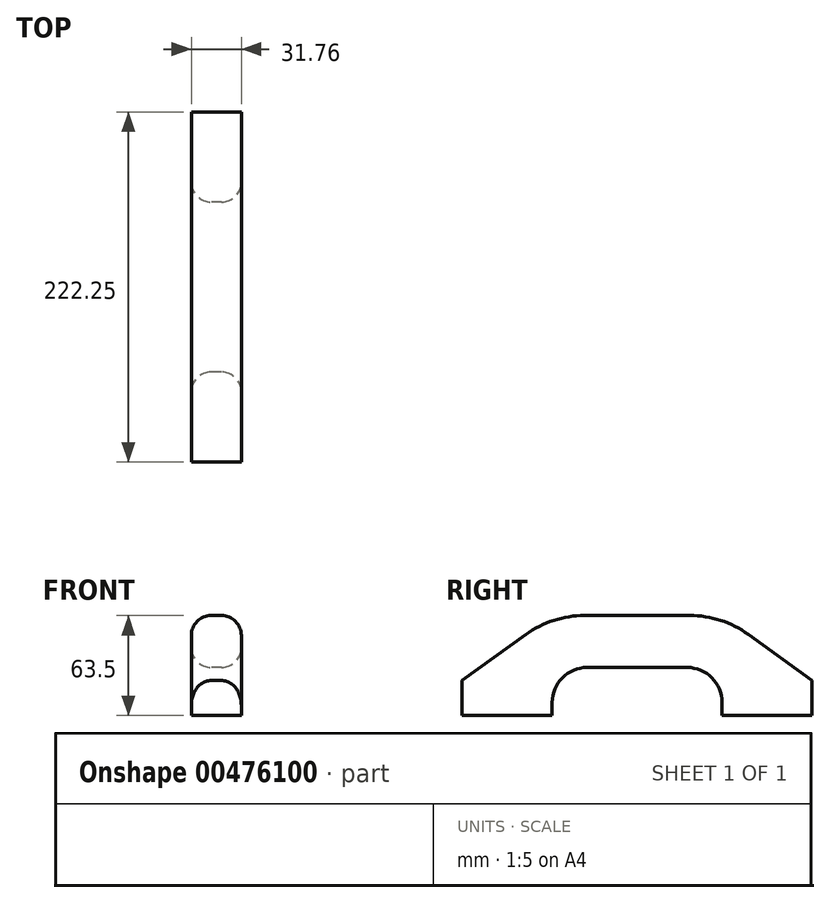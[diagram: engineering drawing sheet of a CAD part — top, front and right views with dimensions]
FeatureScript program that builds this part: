
annotation { "Feature Type Name" : "Feature", "Feature Type Description" : "" }
export const myFeature = defineFeature(function(context is Context, id is Id, definition is map)
    precondition{}
    {
        {
            var Q0;
            Q0=qCreatedBy(makeId("Right.planeOp"),FACE);
            var sketch = newSketch(context, id + "F0", { "sketchPlane" : qUnion([Q0])});
            skLineSegment(sketch, "E0", {"start": v(0, 0) * mm, "end": v(57.15, 0) * mm});
            skLineSegment(sketch, "E1", {"start": v(0, 0) * mm, "end": v(0, 22.23) * mm});
            skLineSegment(sketch, "E2", {"start": v(222.25, 0) * mm, "end": v(222.25, 22.23) * mm});
            skLineSegment(sketch, "E3", {"start": v(57.15, 63.5) * mm, "end": v(165.1, 63.5) * mm});
            skPoint(sketch, "E4", {"position": v(0, 22.23) * mm});
            skPoint(sketch, "E5", {"position": v(222.25, 22.23) * mm});
            skPoint(sketch, "E6", {"position": v(57.15, 0) * mm});
            skPoint(sketch, "E7", {"position": v(165.1, 0) * mm});
            skPoint(sketch, "E8", {"position": v(111.12, 63.5) * mm});
            skLineSegment(sketch, "E9", {"start": v(111.12, 107.02) * mm, "end": v(111.13, -32.56) * mm, "construction": true});
            skPoint(sketch, "E10", {"position": v(111.13, 30.48) * mm});
            skLineSegment(sketch, "E11", {"start": v(111.13, 30.48) * mm, "end": v(57.15, 30.48) * mm});
            skLineSegment(sketch, "E12", {"start": v(57.15, 0) * mm, "end": v(57.15, 30.48) * mm});
            skLineSegment(sketch, "E13", {"start": v(111.13, 30.48) * mm, "end": v(165.1, 30.48) * mm});
            skLineSegment(sketch, "E14", {"start": v(165.1, 0) * mm, "end": v(165.1, 30.48) * mm});
            skLineSegment(sketch, "E15", {"start": v(0, 22.22) * mm, "end": v(57.15, 63.5) * mm});
            skLineSegment(sketch, "E16", {"start": v(222.25, 22.22) * mm, "end": v(165.1, 63.5) * mm});
            skLineSegment(sketch, "E17.trimOffspring", {"start": v(165.1, 0) * mm, "end": v(222.25, 0) * mm});
            skSolve(sketch);
        }
        {
            var Q0;
            Q0=makeQuery(id+"F0.imprint","IMPRINT",FACE,{"disambiguationData":[TD([[makeQuery(id+"F0.imprint","IMPRINT",EDGE,{"derivedFrom":sQuery(id+"F0.wireOp",EDGE,"E0")}),1.0]])]});
            extrude(context, id + "F1", {"entities" : qUnion([Q0]), "flatOperationType" : FlatOperationType.REMOVE, "offsetDistance" : 25.4 * mm, "depth" : 15.88 * mm, "hasSecondDirection" : true, "secondDirectionOppositeDirection" : true, "secondDirectionDepth" : 15.88 * mm, "domain" : OperationDomain.MODEL});
        }
        {
            var Q0;
            Q0=makeQuery(id+"F1.opExtrude","SWEPT_EDGE",EDGE,{"disambiguationData":[OSD([sQuery(id+"F0.wireOp",EDGE,"E3"),sQuery(id+"F0.wireOp",EDGE,"E16")])]});
            var Q1;
            Q1=makeQuery(id+"F1.opExtrude","SWEPT_EDGE",EDGE,{"disambiguationData":[OSD([sQuery(id+"F0.wireOp",EDGE,"E3"),sQuery(id+"F0.wireOp",EDGE,"E15")])]});
            fillet(context, id + "F2", {"entities" : qUnion([Q0, Q1]), "radius" : 63.5 * mm, "tangentPropagation" : true, "allowEdgeOverflow" : false});
        }
        {
            var Q0;
            Q0=makeQuery(id+"F1.opExtrude","SWEPT_EDGE",EDGE,{"disambiguationData":[OSD([sQuery(id+"F0.wireOp",EDGE,"E13"),sQuery(id+"F0.wireOp",EDGE,"E14")])]});
            var Q1;
            Q1=makeQuery(id+"F1.opExtrude","SWEPT_EDGE",EDGE,{"disambiguationData":[OSD([sQuery(id+"F0.wireOp",EDGE,"E11"),sQuery(id+"F0.wireOp",EDGE,"E12")])]});
            fillet(context, id + "F3", {"entities" : qUnion([Q0, Q1]), "radius" : 22.22 * mm, "tangentPropagation" : true, "allowEdgeOverflow" : false});
        }
        {
            var Q0;
            Q0=makeQuery(id+"F1.opExtrude","CAP_EDGE",EDGE,{"disambiguationData":[OSD([sQuery(id+"F0.wireOp",EDGE,"E3")])],"isStart":false});
            var Q1;
            Q1=makeQuery(id+"F1.opExtrude","CAP_EDGE",EDGE,{"disambiguationData":[OSD([sQuery(id+"F0.wireOp",EDGE,"E3")])],"isStart":true});
            var Q2;
            Q2=makeQuery(id+"F1.opExtrude","CAP_EDGE",EDGE,{"disambiguationData":[OSD([sQuery(id+"F0.wireOp",EDGE,"E11"),sQuery(id+"F0.wireOp",EDGE,"E13")])],"isStart":false});
            var Q3;
            Q3=makeQuery(id+"F1.opExtrude","CAP_EDGE",EDGE,{"disambiguationData":[OSD([sQuery(id+"F0.wireOp",EDGE,"E11"),sQuery(id+"F0.wireOp",EDGE,"E13")])],"isStart":true});
            fillet(context, id + "F4", {"entities" : qUnion([Q0, Q1, Q2, Q3]), "radius" : 12.7 * mm, "tangentPropagation" : true, "allowEdgeOverflow" : false});
        }
    });
